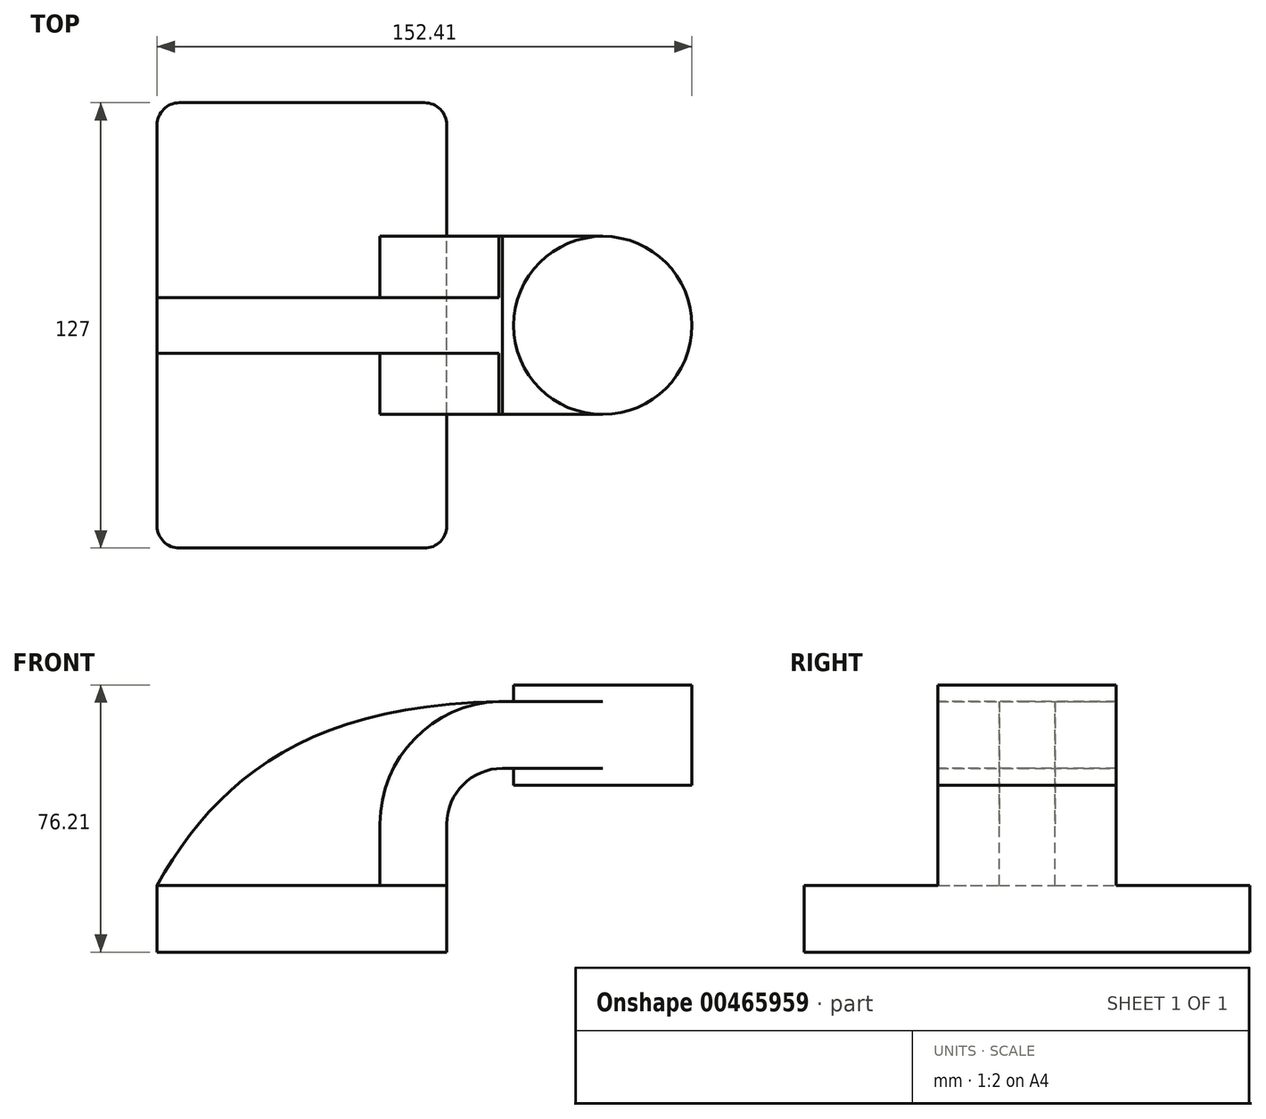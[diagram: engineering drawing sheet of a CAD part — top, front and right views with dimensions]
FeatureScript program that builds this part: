
annotation { "Feature Type Name" : "Feature", "Feature Type Description" : "" }
export const myFeature = defineFeature(function(context is Context, id is Id, definition is map)
    precondition{}
    {
        {
            var Q0;
            Q0=qCreatedBy(makeId("Front.planeOp"),FACE);
            var sketch = newSketch(context, id + "F0", { "sketchPlane" : qUnion([Q0])});
            skLineSegment(sketch, "E0.bottom", {"start": v(-41.28, 9.53) * mm, "end": v(41.28, 9.53) * mm});
            skLineSegment(sketch, "E0.top", {"start": v(-41.28, -9.53) * mm, "end": v(41.28, -9.53) * mm});
            skLineSegment(sketch, "E0.left", {"start": v(-41.28, 9.52) * mm, "end": v(-41.28, -9.53) * mm});
            skLineSegment(sketch, "E0.right", {"start": v(41.27, 9.53) * mm, "end": v(41.28, -9.52) * mm});
            skPoint(sketch, "E0.middle", {"position": v(0, 0) * mm});
            skLineSegment(sketch, "E1.top", {"start": v(60.33, 38.1) * mm, "end": v(111.12, 38.1) * mm});
            skLineSegment(sketch, "E1.left", {"start": v(60.33, 66.67) * mm, "end": v(60.33, 38.1) * mm});
            skLineSegment(sketch, "E1.right", {"start": v(111.12, 66.67) * mm, "end": v(111.13, 38.1) * mm});
            skLineSegment(sketch, "E2", {"start": v(41.27, 9.53) * mm, "end": v(41.27, 27) * mm});
            skArc(sketch, "E3", {"start": v(41.28, 27) * mm, "mid": v(45.92, 38.23) * mm, "end": v(57.15, 42.88) * mm});
            skLineSegment(sketch, "E4", {"start": v(57.15, 42.88) * mm, "end": v(85.72, 42.88) * mm});
            skLineSegment(sketch, "E5", {"start": v(60.33, 66.67) * mm, "end": v(111.12, 66.67) * mm});
            skPoint(sketch, "E6.startSnap0", {"position": v(60.33, 52.39) * mm});
            skPoint(sketch, "E6.startSnap1", {"position": v(85.72, 38.1) * mm});
            skLineSegment(sketch, "E7.0", {"start": v(57.15, 61.93) * mm, "end": v(85.72, 61.93) * mm});
            skArc(sketch, "E7.1", {"start": v(22.23, 27) * mm, "mid": v(32.45, 51.7) * mm, "end": v(57.15, 61.93) * mm});
            skLineSegment(sketch, "E7.2", {"start": v(22.22, 9.53) * mm, "end": v(22.22, 27) * mm});
            skLineSegment(sketch, "E8", {"start": v(85.72, 38.1) * mm, "end": v(85.72, 66.67) * mm});
            skFitSpline(sketch, "E9", {"points": [v(-41.28, 9.52) * mm, v(57.15, 61.93) * mm], "startDerivative": vector(49.11, 86.88) * mm, "endDerivative": vector(171.45, 2.27) * mm});
            skSolve(sketch);
        }
        {
            var Q0;
            Q0=makeQuery(id+"F0.imprint","IMPRINT",FACE,{"disambiguationData":[TD([[makeQuery(id+"F0.imprint","IMPRINT",EDGE,{"derivedFrom":sQuery(id+"F0.wireOp",EDGE,"E0.top")}),1.0]])]});
            extrude(context, id + "F1", {"entities" : qUnion([Q0]), "endBound" : BoundingType.SYMMETRIC, "depth" : 127 * mm});
        }
        {
            var Q0;
            {var subQ1=sQuery(id+"F0.wireOp",EDGE,"E2");Q0=makeQuery(id+"F0.imprint","IMPRINT",FACE,{"disambiguationData":[TD([[makeQuery(id+"F0.imprint","IMPRINT",EDGE,{"derivedFrom":subQ1}),1.0]])]});}
            var Q1;
            {var subQ0=sQuery(id+"F0.wireOp",EDGE,"E7.0");var subQ1=sQuery(id+"F0.wireOp",EDGE,"E1.left");var subQ2=makeQuery(id+"F0.imprint","INTERSECT",VERTEX,{"derivedFrom":[subQ1,subQ0]});Q1=makeQuery(id+"F0.imprint","IMPRINT",FACE,{"disambiguationData":[TD([[makeQuery(id+"F0.imprint","IMPRINT",EDGE,{"disambiguationData":[TD([[subQ2,-1.0]])],"derivedFrom":subQ1}),1.0]])]});}
            extrude(context, id + "F2", {"entities" : qUnion([Q0, Q1]), "operationType" : NewBodyOperationType.ADD, "endBound" : BoundingType.SYMMETRIC, "depth" : 50.8 * mm});
        }
        {
            var Q0;
            {var subQ3=sQuery(id+"F0.wireOp",EDGE,"E7.2");Q0=makeQuery(id+"F0.imprint","IMPRINT",FACE,{"disambiguationData":[TD([[makeQuery(id+"F0.imprint","IMPRINT",EDGE,{"derivedFrom":subQ3}),1.0]])]});}
            extrude(context, id + "F3", {"entities" : qUnion([Q0]), "operationType" : NewBodyOperationType.ADD, "endBound" : BoundingType.SYMMETRIC, "depth" : 15.88 * mm});
        }
        {
            var Q0;
            {var subQ4=sQuery(id+"F0.wireOp",EDGE,"E1.right");Q0=makeQuery(id+"F0.imprint","IMPRINT",FACE,{"disambiguationData":[TD([[makeQuery(id+"F0.imprint","IMPRINT",EDGE,{"derivedFrom":subQ4}),-1.0]])]});}
            var Q1;
            Q1=sQuery(id+"F0.wireOp",EDGE,"E8");
            revolve(context, id + "F4", {"operationType" : NewBodyOperationType.ADD, "entities" : qUnion([Q0]), "axis" : qUnion([Q1]), "revolveType" : RevolveType.FULL});
        }
        {
            var Q0;
            Q0=makeQuery(id+"F1.opExtrude","CAP_EDGE",EDGE,{"disambiguationData":[OSD([sQuery(id+"F0.wireOp",EDGE,"E0.right")])],"isStart":true});
            var Q1;
            Q1=makeQuery(id+"F1.opExtrude","CAP_EDGE",EDGE,{"disambiguationData":[OSD([sQuery(id+"F0.wireOp",EDGE,"E0.left")])],"isStart":true});
            var Q2;
            Q2=makeQuery(id+"F1.opExtrude","CAP_EDGE",EDGE,{"disambiguationData":[OSD([sQuery(id+"F0.wireOp",EDGE,"E0.right")])],"isStart":false});
            var Q3;
            Q3=makeQuery(id+"F1.opExtrude","CAP_EDGE",EDGE,{"disambiguationData":[OSD([sQuery(id+"F0.wireOp",EDGE,"E0.left")])],"isStart":false});
            fillet(context, id + "F5", {"entities" : qUnion([Q0, Q1, Q2, Q3]), "radius" : 6.35 * mm, "tangentPropagation" : true, "allowEdgeOverflow" : false});
        }
    });
